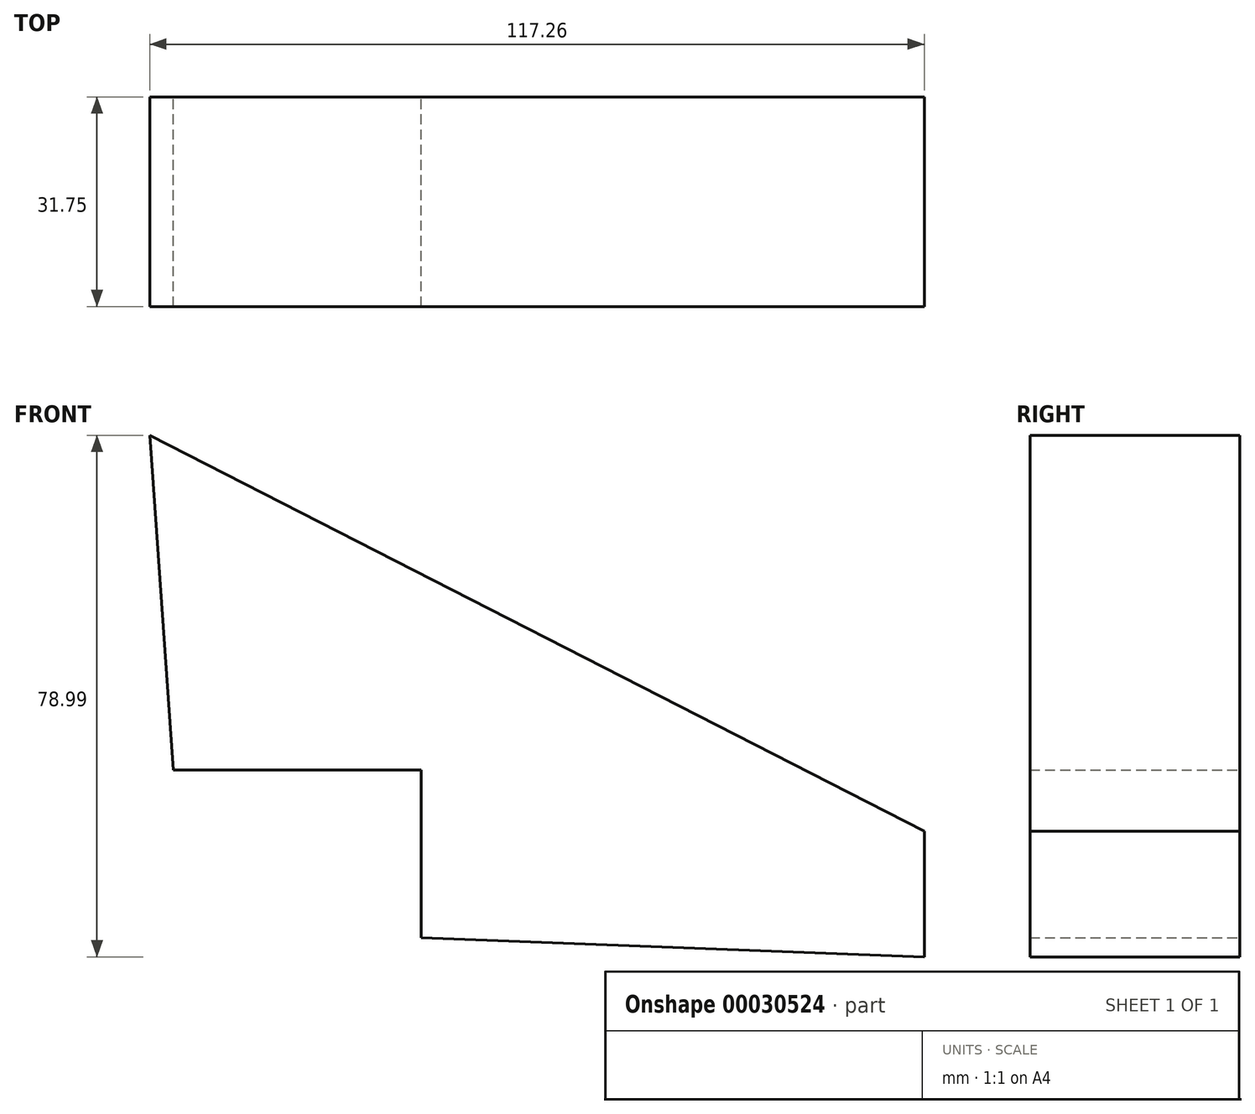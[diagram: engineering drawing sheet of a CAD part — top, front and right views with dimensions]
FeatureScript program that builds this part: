
annotation { "Feature Type Name" : "Feature", "Feature Type Description" : "" }
export const myFeature = defineFeature(function(context is Context, id is Id, definition is map)
    precondition{}
    {
        {
            var Q0;
            Q0=qCreatedBy(makeId("Front.planeOp"),FACE);
            var sketch = newSketch(context, id + "F0", { "sketchPlane" : qUnion([Q0])});
            skLineSegment(sketch, "E0", {"start": v(-57.14, 38.87) * mm, "end": v(-53.57, -11.8) * mm});
            skLineSegment(sketch, "E1", {"start": v(-53.57, -11.8) * mm, "end": v(-16.02, -11.8) * mm});
            skLineSegment(sketch, "E2", {"start": v(-16.02, -11.8) * mm, "end": v(-16.02, -37.2) * mm});
            skLineSegment(sketch, "E3", {"start": v(-16.02, -37.2) * mm, "end": v(60.12, -40.12) * mm});
            skLineSegment(sketch, "E4", {"start": v(60.12, -40.12) * mm, "end": v(60.12, -21.07) * mm});
            skLineSegment(sketch, "E5", {"start": v(-57.14, 38.87) * mm, "end": v(60.12, -21.07) * mm});
            skSolve(sketch);
        }
        {
            var Q0;
            Q0=makeQuery(id+"F0.imprint","IMPRINT",FACE,{"disambiguationData":[TD([[makeQuery(id+"F0.imprint","IMPRINT",EDGE,{"derivedFrom":sQuery(id+"F0.wireOp",EDGE,"E0")}),1.0]])]});
            extrude(context, id + "F1", {"entities" : qUnion([Q0]), "depth" : 31.75 * mm});
        }
    });
